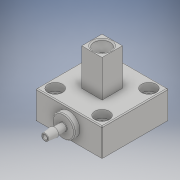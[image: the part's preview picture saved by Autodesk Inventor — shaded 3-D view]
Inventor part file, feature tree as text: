
AUTODESK INVENTOR PART (.ipt)
format: ipt  version: 2019 (Build 230136000, 136)  size: 289,792 bytes
history: native  units: mm
features: sketch x8, plane x3, extrude x3, revolve x2, fillet x2, sweep x1, hole x1, projected_geometry x1
ambient origin geometry x8: Origin, YZ Plane, XZ Plane, XY Plane, X Axis, Y Axis, Z Axis, Center Point
bodies: Solid1 (feature_tree)
feature tree (21):
  revolve  "Revolution1"  [1 undecoded]
  plane  "Work Plane1"
  extrude  "Extrusion1"  Depth=0.35mm
  plane  "Work Plane7"
  extrude  "Extrusion6"  Depth=0.75mm
  extrude  "Extrusion7"  TaperAngle=90.0deg  [1 undecoded]
  sketch  "Sketch17"  dims[d11=0.0mm d14=2.0mm d15=0.0mm d45=0.0mm]
  plane  "Work Plane8"
  sweep  "Sweep3"
  fillet  "Fillet1"  [1 undecoded]
  hole  "Hole3"  [1 undecoded]
  revolve  "Revolution2"  [1 undecoded]
  fillet  "Fillet2"  Radius=32.7mm
  sketch  "Sketch1"  dims[d0=5.5mm d1=20.0mm]
  sketch  "Sketch2"  dims[d5=9.0mm d6=0.35mm]
  sketch  "Sketch11"  dims[d7=0.75mm d8=0.75mm]
  sketch  "Sketch16"  dims[d9=0.75mm d10=90.0deg]
  projected_geometry  "Projected Loop9"
  sketch  "Sketch18"  dims[d47=15.0mm d48=0.0mm d60=36.0mm]
  sketch  "Sketch19"  dims[d61=36.0mm d64=8.45mm d65=32.7mm d66=0.0mm]
  sketch  "Sketch21"  dims[d67=0.0mm d68=0.0mm d69=3.0mm d70=25.4mm d71=25.4mm d72=4.496mm d73=6.0mm d74=7.938mm d75=4.166mm d76=90.0deg d77=19.05mm d78=20.594885mm d79=3.0mm d80=6.0mm d81=5.0mm d82=1.8796mm d83=0.25mm d84=2.413mm d85=5.08mm d86=1.15mm d87=0.25mm d88=0.25mm d89=90.0deg d90=0.5mm d124=0.0mm]
note: 5 required parameter values undecoded (feature->parameter linkage not recoverable at this tier; creation-order binding heuristic only, values carry confidence <= 0.55)